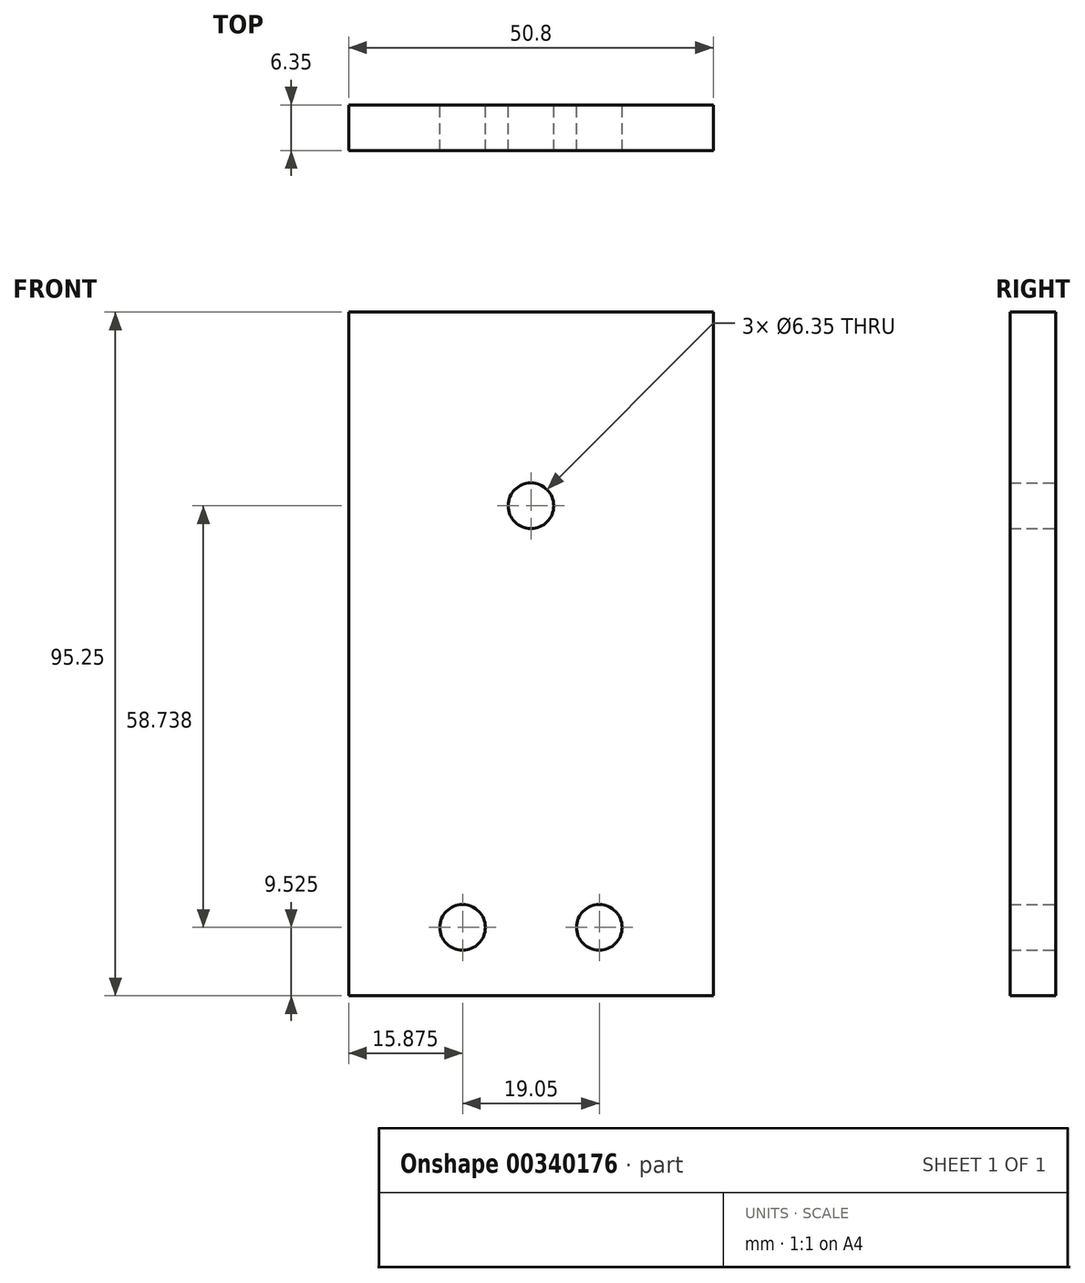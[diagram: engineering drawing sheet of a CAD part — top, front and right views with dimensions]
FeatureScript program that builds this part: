
annotation { "Feature Type Name" : "Feature", "Feature Type Description" : "" }
export const myFeature = defineFeature(function(context is Context, id is Id, definition is map)
    precondition{}
    {
        {
            var Q0;
            Q0=qCreatedBy(makeId("Front.planeOp"),FACE);
            var sketch = newSketch(context, id + "F0", { "sketchPlane" : qUnion([Q0])});
            skLineSegment(sketch, "E0.bottom", {"start": v(0, 0) * mm, "end": v(50.8, 0) * mm});
            skLineSegment(sketch, "E0.top", {"start": v(0, 95.25) * mm, "end": v(50.8, 95.25) * mm});
            skLineSegment(sketch, "E0.left", {"start": v(0, 0) * mm, "end": v(0, 95.25) * mm});
            skLineSegment(sketch, "E0.right", {"start": v(50.8, 0) * mm, "end": v(50.8, 95.25) * mm});
            skLineSegment(sketch, "E1", {"start": v(25.4, 95.25) * mm, "end": v(25.4, 9.52) * mm});
            skLineSegment(sketch, "E2", {"start": v(15.87, 9.52) * mm, "end": v(34.92, 9.52) * mm});
            skCircle(sketch, "E3", {"center": v(25.4, 68.26) * mm, "radius": 3.18 * mm});
            skCircle(sketch, "E4", {"center": v(34.92, 9.52) * mm, "radius": 3.18 * mm});
            skCircle(sketch, "E5", {"center": v(15.87, 9.52) * mm, "radius": 3.18 * mm});
            skSolve(sketch);
        }
        {
            var Q0;
            Q0 = qSketchRegion(id + "F0", true);
            extrude(context, id + "F1", {"entities" : qUnion([Q0]), "depth" : 6.35 * mm});
        }
    });
